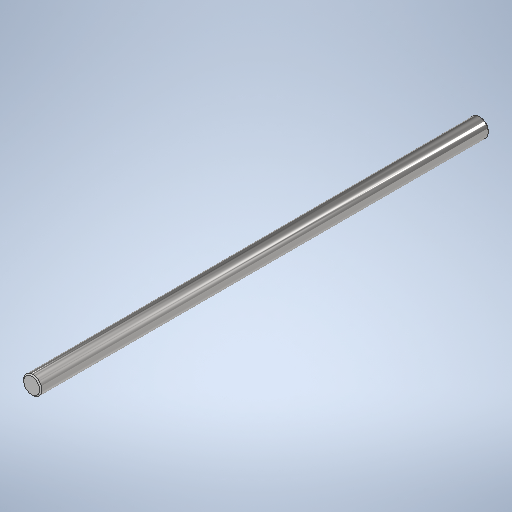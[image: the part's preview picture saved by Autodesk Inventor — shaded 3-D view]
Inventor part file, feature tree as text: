
AUTODESK INVENTOR PART (.ipt)
format: ipt  version: 2025.2 (Build 292293000, 293)  size: 259,072 bytes
history: native  units: mm
features: extrude x1, chamfer x1, sketch x1
ambient origin geometry x8: Origin, YZ Plane, XZ Plane, XY Plane, X Axis, Y Axis, Z Axis, Center Point
bodies: Solid1 (feature_tree)
feature tree (3):
  extrude  "Extrusion1"  Depth=195.0mm TaperAngle=0.0deg
  chamfer  "Chamfer1"  Distance=0.5mm Angle=45.0deg
  sketch  "Sketch1"  dims[d0=8.0mm d1=195.0mm d2=0.0mm d3=0.5mm d4=2.0mm d5=45.0deg]
